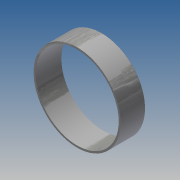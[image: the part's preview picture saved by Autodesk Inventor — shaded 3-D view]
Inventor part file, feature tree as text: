
AUTODESK INVENTOR PART (.ipt)
format: ipt  version: 2017.3 (Build 213257000, 257)  size: 165,888 bytes
history: native  units: in
note: dims shown in document units (in); Inventor stores cm internally (conversion verified against a paired STEP export)
features: chamfer x2, plane x2, split x2, extrude x1, sketch x1
ambient origin geometry x8: Origin, YZ Plane, XZ Plane, XY Plane, X Axis, Y Axis, Z Axis, Center Point
bodies: Solid1 (feature_tree)
feature tree (8):
  extrude  "Extrusion1"  Depth=10.0938in
  chamfer  "Chamfer1"  Distance=10.0938in
  plane  "Work Plane2"
  split  "Split1"
  split  "Split2"
  chamfer  "Chamfer2"  Distance=0.6875in
  sketch  "Sketch1"  dims[d0=34.0in d1=32.5in d2=10.0938in d3=0.0in d4=0.6875in d5=0.125in d6=0.2577in d7=-2.0in d8=0.75in d9=0.0312in d10=0.125in d11=45.0deg]
  plane  "Work Plane1"
